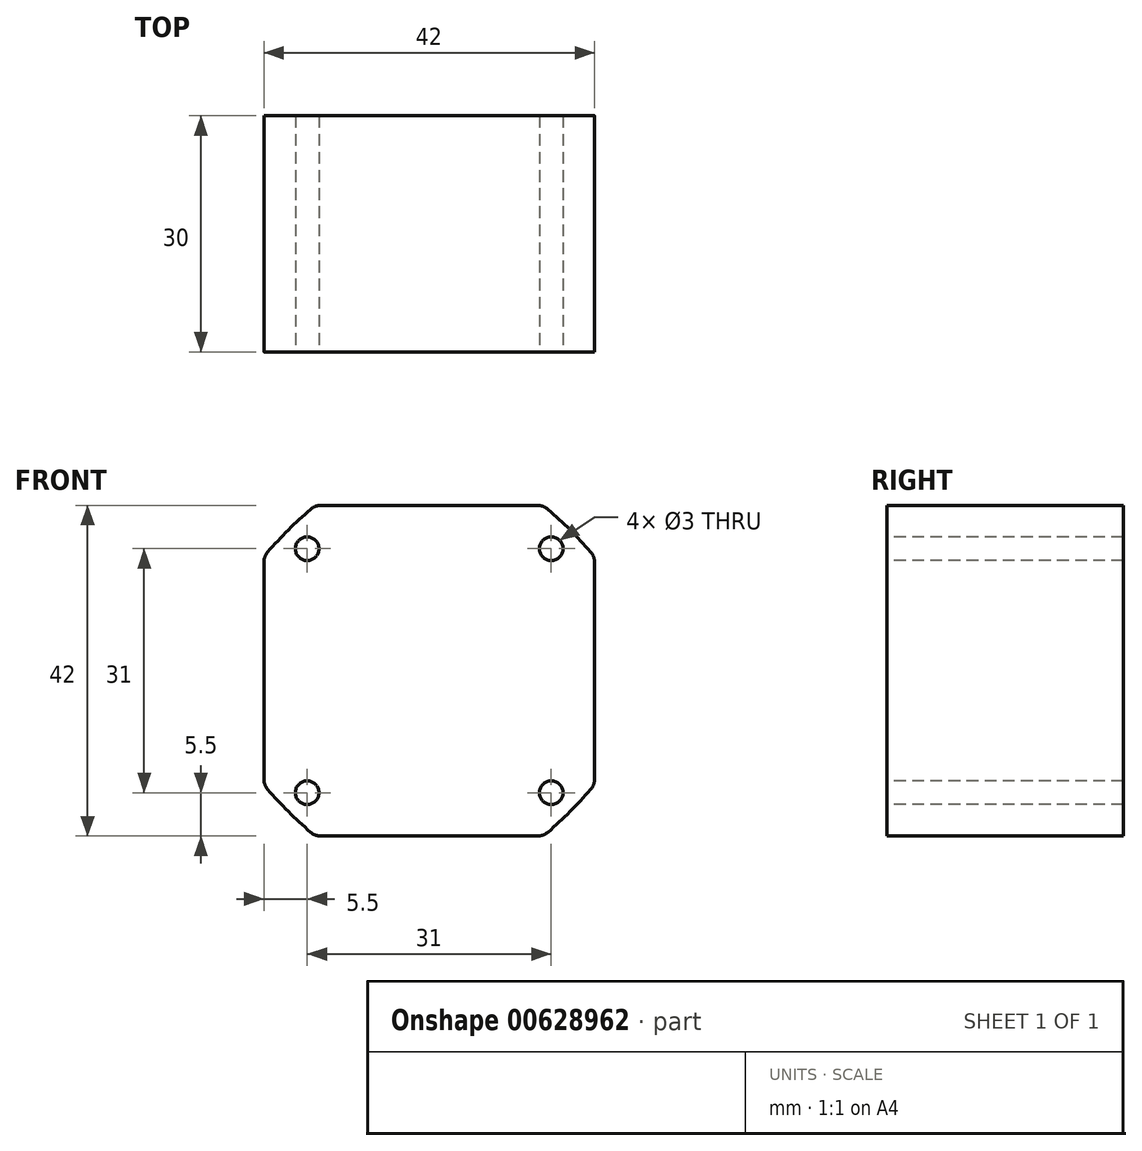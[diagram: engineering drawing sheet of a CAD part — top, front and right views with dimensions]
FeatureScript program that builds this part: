
annotation { "Feature Type Name" : "Feature", "Feature Type Description" : "" }
export const myFeature = defineFeature(function(context is Context, id is Id, definition is map)
    precondition{}
    {
        {
            var Q0;
            Q0=qCreatedBy(makeId("Front.planeOp"),FACE);
            var sketch = newSketch(context, id + "F0", { "sketchPlane" : qUnion([Q0])});
            skLineSegment(sketch, "E0.bottom", {"start": v(-21, 21) * mm, "end": v(21, 21) * mm, "construction": true});
            skLineSegment(sketch, "E0.top", {"start": v(-21, -21) * mm, "end": v(21, -21) * mm, "construction": true});
            skLineSegment(sketch, "E0.left", {"start": v(-21, 21) * mm, "end": v(-21, -21) * mm, "construction": true});
            skLineSegment(sketch, "E0.right", {"start": v(21, 21) * mm, "end": v(21, -21) * mm, "construction": true});
            skPoint(sketch, "E0.middle", {"position": v(0, 0) * mm});
            skArc(sketch, "E1", {"start": v(-21, 14.51) * mm, "mid": v(-17.9, 17.9) * mm, "end": v(-14.51, 21) * mm});
            skArc(sketch, "E2.1.0", {"start": v(-14.51, -21) * mm, "mid": v(-17.9, -17.9) * mm, "end": v(-21, -14.51) * mm});
            skArc(sketch, "E2.2.0", {"start": v(21, -14.51) * mm, "mid": v(17.9, -17.9) * mm, "end": v(14.51, -21) * mm});
            skArc(sketch, "E2.3.0", {"start": v(14.51, 21) * mm, "mid": v(17.9, 17.9) * mm, "end": v(21, 14.51) * mm});
            skLineSegment(sketch, "E3", {"start": v(-14.51, 21) * mm, "end": v(14.51, 21) * mm});
            skLineSegment(sketch, "E4", {"start": v(21, 14.51) * mm, "end": v(21, -14.51) * mm});
            skLineSegment(sketch, "E5", {"start": v(14.51, -21) * mm, "end": v(-14.51, -21) * mm});
            skLineSegment(sketch, "E6", {"start": v(-21, -14.51) * mm, "end": v(-21, 14.51) * mm});
            skSolve(sketch);
        }
        {
            var Q0;
            Q0=qSketchRegion(id+"F0",true);
            extrude(context, id + "F1", {"entities" : qUnion([Q0]), "endBound" : BoundingType.SYMMETRIC, "depth" : 30 * mm, "offsetDistance" : 25 * mm});
        }
        {
            var Q0;
            Q0=makeQuery(id+"F1.opExtrude","SWEPT_EDGE",EDGE,{"disambiguationData":[OSD([sQuery(id+"F0.wireOp",EDGE,"E2.3.0"),sQuery(id+"F0.wireOp",EDGE,"E3")])]});
            var Q1;
            Q1=makeQuery(id+"F1.opExtrude","SWEPT_EDGE",EDGE,{"disambiguationData":[OSD([sQuery(id+"F0.wireOp",EDGE,"E2.3.0"),sQuery(id+"F0.wireOp",EDGE,"E4")])]});
            var Q2;
            Q2=makeQuery(id+"F1.opExtrude","SWEPT_EDGE",EDGE,{"disambiguationData":[OSD([sQuery(id+"F0.wireOp",EDGE,"E2.2.0"),sQuery(id+"F0.wireOp",EDGE,"E4")])]});
            var Q3;
            Q3=makeQuery(id+"F1.opExtrude","SWEPT_EDGE",EDGE,{"disambiguationData":[OSD([sQuery(id+"F0.wireOp",EDGE,"E2.2.0"),sQuery(id+"F0.wireOp",EDGE,"E5")])]});
            var Q4;
            Q4=makeQuery(id+"F1.opExtrude","SWEPT_EDGE",EDGE,{"disambiguationData":[OSD([sQuery(id+"F0.wireOp",EDGE,"E2.1.0"),sQuery(id+"F0.wireOp",EDGE,"E5")])]});
            var Q5;
            Q5=makeQuery(id+"F1.opExtrude","SWEPT_EDGE",EDGE,{"disambiguationData":[OSD([sQuery(id+"F0.wireOp",EDGE,"E2.1.0"),sQuery(id+"F0.wireOp",EDGE,"E6")])]});
            var Q6;
            Q6=makeQuery(id+"F1.opExtrude","SWEPT_EDGE",EDGE,{"disambiguationData":[OSD([sQuery(id+"F0.wireOp",EDGE,"E1"),sQuery(id+"F0.wireOp",EDGE,"E6")])]});
            var Q7;
            Q7=makeQuery(id+"F1.opExtrude","SWEPT_EDGE",EDGE,{"disambiguationData":[OSD([sQuery(id+"F0.wireOp",EDGE,"E1"),sQuery(id+"F0.wireOp",EDGE,"E3")])]});
            fillet(context, id + "F2", {"entities" : qUnion([Q0, Q1, Q2, Q3, Q4, Q5, Q6, Q7]), "radius" : 2 * mm, "tangentPropagation" : true, "allowEdgeOverflow" : false});
        }
        {
            var Q0;
            Q0=makeQuery(id+"F1.opExtrude","CAP_FACE",FACE,{"disambiguationData":[OSD([sQuery(id+"F0.wireOp",EDGE,"E1"),sQuery(id+"F0.wireOp",EDGE,"E2.1.0"),sQuery(id+"F0.wireOp",EDGE,"E2.2.0"),sQuery(id+"F0.wireOp",EDGE,"E2.3.0"),sQuery(id+"F0.wireOp",EDGE,"E3"),sQuery(id+"F0.wireOp",EDGE,"E4"),sQuery(id+"F0.wireOp",EDGE,"E5"),sQuery(id+"F0.wireOp",EDGE,"E6")])],"isStart":false});
            var sketch = newSketch(context, id + "F3", { "sketchPlane" : qUnion([Q0])});
            skCircle(sketch, "E7", {"center": v(15.5, 15.5) * mm, "radius": 1.5 * mm});
            skCircle(sketch, "E8.1.0", {"center": v(-15.5, 15.5) * mm, "radius": 1.5 * mm});
            skCircle(sketch, "E8.2.0", {"center": v(-15.5, -15.5) * mm, "radius": 1.5 * mm});
            skCircle(sketch, "E8.3.0", {"center": v(15.5, -15.5) * mm, "radius": 1.5 * mm});
            skPoint(sketch, "E8.center", {"position": v(0, 0) * mm});
            skSolve(sketch);
        }
        {
            var Q0;
            Q0=qSketchRegion(id+"F3",true);
            extrude(context, id + "F4", {"entities" : qUnion([Q0]), "operationType" : NewBodyOperationType.REMOVE, "endBound" : BoundingType.THROUGH_ALL, "oppositeDirection" : true, "depth" : 25 * mm, "offsetDistance" : 25 * mm});
        }
    });
